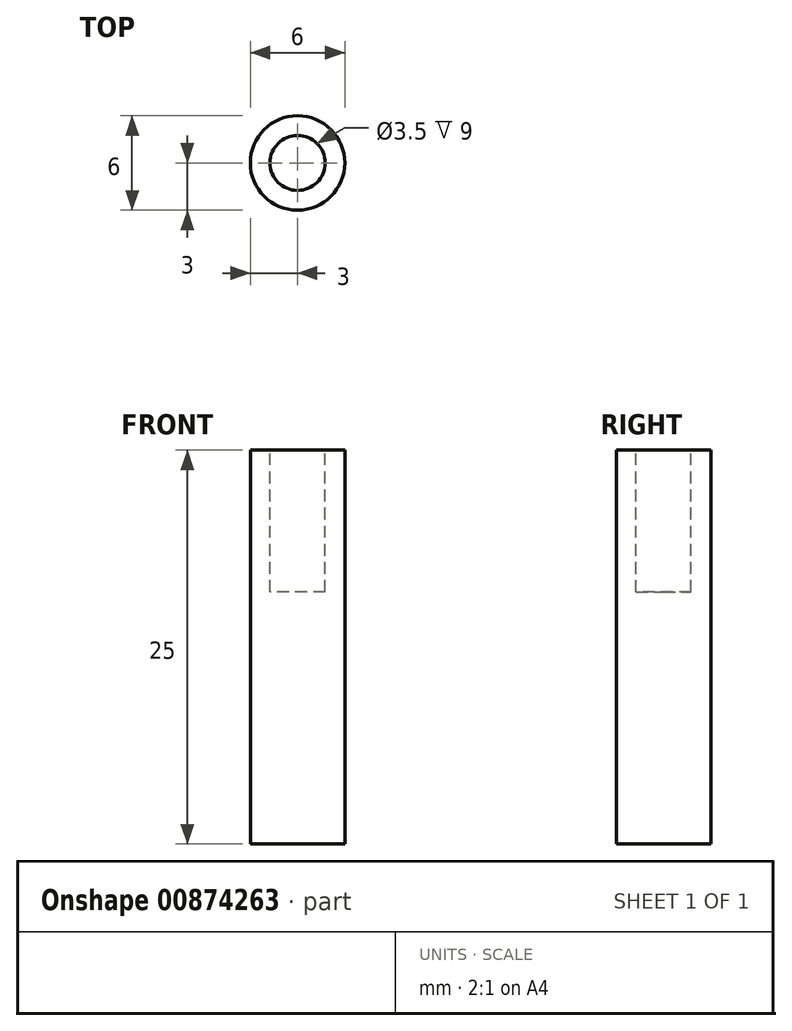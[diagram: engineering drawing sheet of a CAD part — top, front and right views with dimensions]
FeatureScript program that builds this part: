
annotation { "Feature Type Name" : "Feature", "Feature Type Description" : "" }
export const myFeature = defineFeature(function(context is Context, id is Id, definition is map)
    precondition{}
    {
        {
            var Q0;
            Q0=qCreatedBy(makeId("Top.planeOp"),FACE);
            var sketch = newSketch(context, id + "F0", { "sketchPlane" : qUnion([Q0])});
            skCircle(sketch, "E0", {"center": v(0, 0) * mm, "radius": 3 * mm});
            skCircle(sketch, "E1", {"center": v(0, 0) * mm, "radius": 1.75 * mm});
            skSolve(sketch);
        }
        {
            var Q0;
            Q0=makeQuery(id+"F0.imprint","IMPRINT",FACE,{"disambiguationData":[TD([[makeQuery(id+"F0.imprint","IMPRINT",EDGE,{"derivedFrom":sQuery(id+"F0.wireOp",EDGE,"E0")}),1.0]])]});
            var Q1;
            Q1=makeQuery(id+"F0.imprint","IMPRINT",FACE,{"disambiguationData":[TD([[makeQuery(id+"F0.imprint","IMPRINT",EDGE,{"derivedFrom":sQuery(id+"F0.wireOp",EDGE,"E1")}),1.0]])]});
            extrude(context, id + "F1", {"entities" : qUnion([Q0, Q1]), "endBound" : BoundingType.SYMMETRIC, "depth" : 25 * mm, "offsetDistance" : 25 * mm});
        }
        {
            var Q0;
            Q0=makeQuery(id+"F1.opExtrude","CAP_FACE",FACE,{"disambiguationData":[OSD([sQuery(id+"F0.wireOp",EDGE,"E0")])],"isStart":false});
            cPlane(context, id + "F2", {"entities" : qUnion([Q0]), "cplaneType" : CPlaneType.OFFSET, "offset" : 0 * mm, "width" : 150 * mm, "height" : 150 * mm});
        }
        {
            var Q0;
            Q0=qCreatedBy(id+"F2.planeOp",FACE);
            var sketch = newSketch(context, id + "F3", { "sketchPlane" : qUnion([Q0])});
            skCircle(sketch, "E2", {"center": v(0, 0) * mm, "radius": 1.75 * mm});
            skSolve(sketch);
        }
        {
            var Q0;
            Q0=makeQuery(id+"F3.imprint","IMPRINT",FACE,{"disambiguationData":[TD([[makeQuery(id+"F3.imprint","IMPRINT",EDGE,{"derivedFrom":sQuery(id+"F3.wireOp",EDGE,"E2")}),1.0]])]});
            extrude(context, id + "F4", {"entities" : qUnion([Q0]), "operationType" : NewBodyOperationType.REMOVE, "oppositeDirection" : true, "depth" : 9 * mm, "offsetDistance" : 25 * mm});
        }
    });
